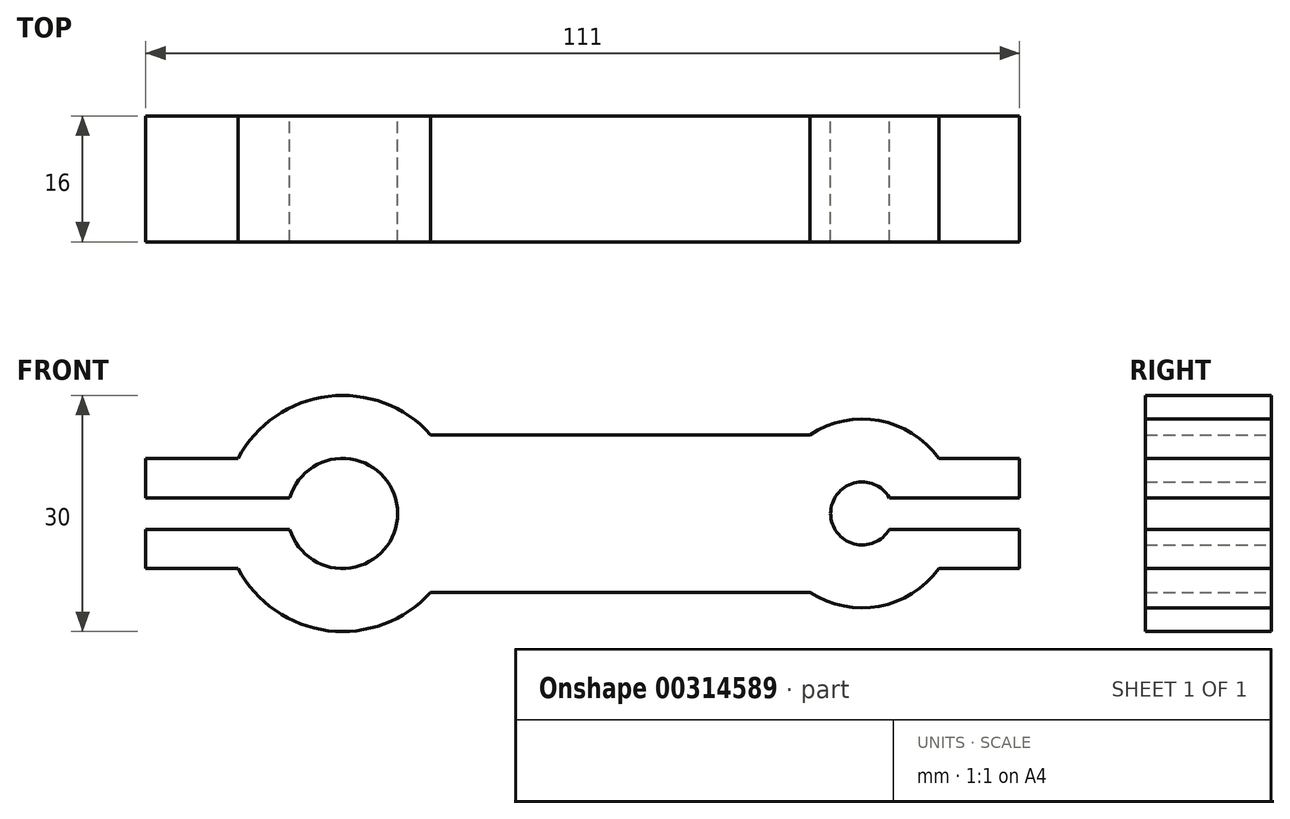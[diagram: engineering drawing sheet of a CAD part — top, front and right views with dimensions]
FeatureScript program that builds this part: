
annotation { "Feature Type Name" : "Feature", "Feature Type Description" : "" }
export const myFeature = defineFeature(function(context is Context, id is Id, definition is map)
    precondition{}
    {
        {
            var Q0;
            Q0=qCreatedBy(makeId("Front.planeOp"),FACE);
            var sketch = newSketch(context, id + "F0", { "sketchPlane" : qUnion([Q0])});
            skArc(sketch, "E0", {"start": v(-11.63, -2) * mm, "mid": v(2.07, 0) * mm, "end": v(-11.63, 2) * mm});
            skArc(sketch, "E1", {"start": v(64.54, 2) * mm, "mid": v(57.07, 0) * mm, "end": v(64.54, -2) * mm});
            skLineSegment(sketch, "E2", {"start": v(2.07, 0) * mm, "end": v(57.07, 0) * mm, "construction": true});
            skArc(sketch, "E3", {"start": v(-19.8, -2) * mm, "mid": v(10.07, 0) * mm, "end": v(-19.8, 2) * mm});
            skArc(sketch, "E4", {"start": v(72.9, 2) * mm, "mid": v(49.07, 0) * mm, "end": v(72.9, -2) * mm});
            skLineSegment(sketch, "E5", {"start": v(6.26, 10) * mm, "end": v(54.44, 10) * mm});
            skLineSegment(sketch, "E6", {"start": v(54.44, -10) * mm, "end": v(6.26, -10) * mm});
            skLineSegment(sketch, "E7", {"start": v(70.82, -7) * mm, "end": v(81.07, -7) * mm});
            skLineSegment(sketch, "E8", {"start": v(81.07, -7) * mm, "end": v(81.07, -2) * mm});
            skLineSegment(sketch, "E9", {"start": v(81.07, -2) * mm, "end": v(64.54, -2) * mm});
            skLineSegment(sketch, "E10", {"start": v(64.54, 2) * mm, "end": v(81.07, 2) * mm});
            skLineSegment(sketch, "E11", {"start": v(81.07, 2) * mm, "end": v(81.07, 7) * mm});
            skLineSegment(sketch, "E12", {"start": v(81.07, 7) * mm, "end": v(70.82, 7) * mm});
            skLineSegment(sketch, "E13", {"start": v(-18.2, -7) * mm, "end": v(-29.93, -7) * mm});
            skLineSegment(sketch, "E14", {"start": v(-29.93, -7) * mm, "end": v(-29.93, -2) * mm});
            skLineSegment(sketch, "E15", {"start": v(-29.93, 2) * mm, "end": v(-29.93, 7) * mm});
            skLineSegment(sketch, "E16", {"start": v(-29.93, 7) * mm, "end": v(-18.2, 7) * mm});
            skLineSegment(sketch, "E17", {"start": v(-29.93, 2) * mm, "end": v(-11.63, 2) * mm});
            skLineSegment(sketch, "E18", {"start": v(-29.93, -2) * mm, "end": v(-11.63, -2) * mm});
            skSolve(sketch);
        }
        {
            var Q0;
            Q0 = qSketchRegion(id + "F0", true);
            extrude(context, id + "F1", {"entities" : qUnion([Q0]), "depth" : 16 * mm});
        }
    });
